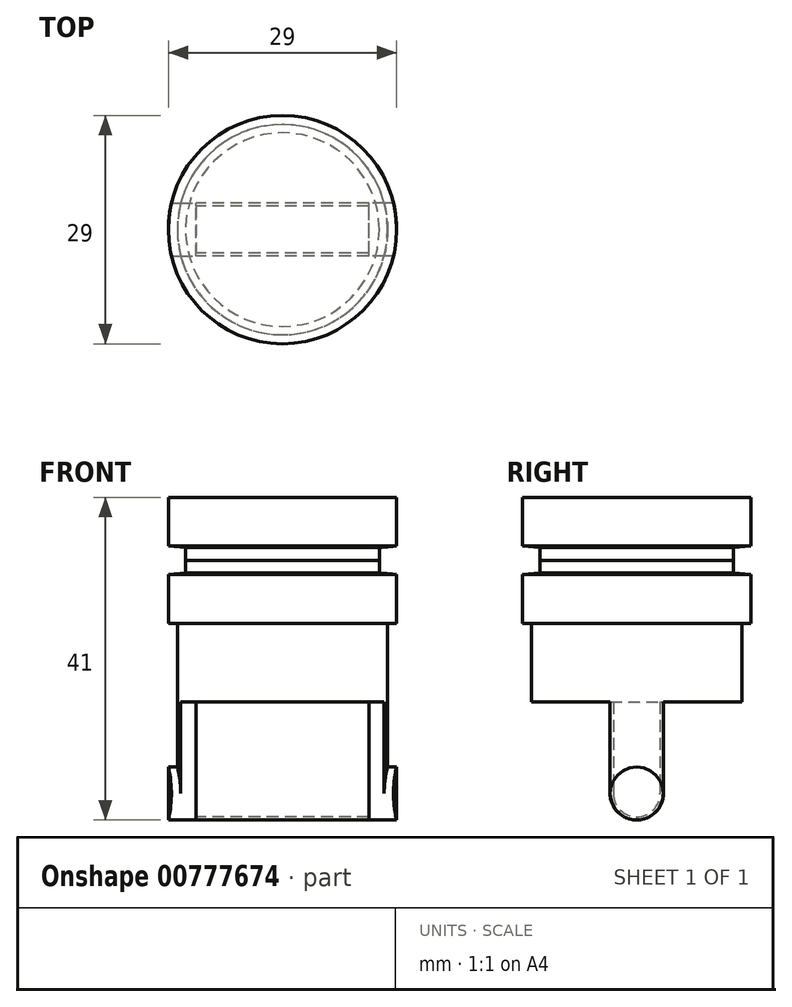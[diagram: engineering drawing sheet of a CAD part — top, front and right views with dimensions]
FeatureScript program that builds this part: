
annotation { "Feature Type Name" : "Feature", "Feature Type Description" : "" }
export const myFeature = defineFeature(function(context is Context, id is Id, definition is map)
    precondition{}
    {
        {
            var Q0;
            Q0=qCreatedBy(makeId("Top.planeOp"),FACE);
            var sketch = newSketch(context, id + "F0", { "sketchPlane" : qUnion([Q0])});
            skCircle(sketch, "E0", {"center": v(0, 0) * mm, "radius": 13.35 * mm});
            skCircle(sketch, "E1", {"center": v(0, 0) * mm, "radius": 14.5 * mm});
            skSolve(sketch);
        }
        {
            var Q0;
            Q0=makeQuery(id+"F0.imprint","IMPRINT",FACE,{"disambiguationData":[TD([[makeQuery(id+"F0.imprint","IMPRINT",EDGE,{"derivedFrom":sQuery(id+"F0.wireOp",EDGE,"E0")}),1.0]])]});
            extrude(context, id + "F1", {"entities" : qUnion([Q0]), "oppositeDirection" : true, "depth" : 10 * mm, "offsetDistance" : 25 * mm});
        }
        {
            var Q0;
            Q0=makeQuery(id+"F0.imprint","IMPRINT",FACE,{"disambiguationData":[TD([[makeQuery(id+"F0.imprint","IMPRINT",EDGE,{"derivedFrom":sQuery(id+"F0.wireOp",EDGE,"E0")}),1.0]])]});
            var Q1;
            Q1=makeQuery(id+"F0.imprint","IMPRINT",FACE,{"disambiguationData":[TD([[makeQuery(id+"F0.imprint","IMPRINT",EDGE,{"derivedFrom":sQuery(id+"F0.wireOp",EDGE,"E0")}),-1.0]])]});
            extrude(context, id + "F2", {"entities" : qUnion([Q0, Q1]), "operationType" : NewBodyOperationType.ADD, "depth" : 8 * mm, "offsetDistance" : 25 * mm});
        }
        {
            var Q0;
            Q0=makeQuery(id+"F2.opExtrude","CAP_FACE",FACE,{"disambiguationData":[OSD([sQuery(id+"F0.wireOp",EDGE,"E1")])],"isStart":false});
            extrude(context, id + "F3", {"entities" : qUnion([Q0]), "depth" : 8 * mm, "offsetDistance" : 25 * mm});
        }
        {
            var Q0;
            Q0=qCreatedBy(makeId("Front.planeOp"),FACE);
            var sketch = newSketch(context, id + "F4", { "sketchPlane" : qUnion([Q0])});
            skLineSegment(sketch, "E2.0", {"start": v(-14.5, 8) * mm, "end": v(14.5, 8) * mm});
            skLineSegment(sketch, "E3.bottom", {"start": v(-14.5, 6.18) * mm, "end": v(-12.3, 6.37) * mm});
            skLineSegment(sketch, "E3.top", {"start": v(-14.5, 9.82) * mm, "end": v(-12.3, 9.63) * mm});
            skLineSegment(sketch, "E3.left", {"start": v(-14.5, 6.18) * mm, "end": v(-14.5, 9.82) * mm});
            skLineSegment(sketch, "E3.right", {"start": v(-12.3, 6.37) * mm, "end": v(-12.3, 9.63) * mm});
            skSolve(sketch);
        }
        {
            var Q0;
            {var subQ5=sQuery(id+"F4.wireOp",EDGE,"E3.top");Q0=makeQuery(id+"F4.imprint","IMPRINT",FACE,{"disambiguationData":[TD([[makeQuery(id+"F4.imprint","IMPRINT",EDGE,{"derivedFrom":subQ5}),-1.0]])]});}
            var Q1;
            {var subQ5=sQuery(id+"F4.wireOp",EDGE,"E3.bottom");Q1=makeQuery(id+"F4.imprint","IMPRINT",FACE,{"disambiguationData":[TD([[makeQuery(id+"F4.imprint","IMPRINT",EDGE,{"derivedFrom":subQ5}),1.0]])]});}
            var Q2;
            Q2=makeQuery(id+"F2.opExtrude","CAP_EDGE",EDGE,{"disambiguationData":[OSD([sQuery(id+"F0.wireOp",EDGE,"E1")])],"isStart":false});
            revolve(context, id + "F5", {"operationType" : NewBodyOperationType.REMOVE, "surfaceOperationType" : NewSurfaceOperationType.NEW, "entities" : qUnion([Q0, Q1]), "axis" : qUnion([Q2]), "revolveType" : RevolveType.FULL, "oppositeDirection" : true});
        }
        {
            var Q0;
            Q0=qCreatedBy(makeId("Right.planeOp"),FACE);
            cPlane(context, id + "F6", {"entities" : qUnion([Q0]), "cplaneType" : CPlaneType.OFFSET, "offset" : 11 * mm, "width" : 150 * mm, "height" : 150 * mm});
        }
        {
            var Q0;
            Q0=qCreatedBy(id+"F6.planeOp",FACE);
            var sketch = newSketch(context, id + "F7", { "sketchPlane" : qUnion([Q0])});
            skLineSegment(sketch, "E4.0", {"start": v(-13.35, -10) * mm, "end": v(13.35, -10) * mm});
            skLineSegment(sketch, "E5.bottom", {"start": v(-3.38, -10) * mm, "end": v(3.38, -10) * mm});
            skLineSegment(sketch, "E5.top", {"start": v(-3.38, -25) * mm, "end": v(3.38, -25) * mm});
            skLineSegment(sketch, "E5.left", {"start": v(-3.37, -10) * mm, "end": v(-3.38, -25) * mm});
            skLineSegment(sketch, "E5.right", {"start": v(3.38, -10) * mm, "end": v(3.37, -25) * mm});
            skPoint(sketch, "E6", {"position": v(0, -25) * mm});
            skPoint(sketch, "E6.positionSnap0", {"position": v(0, -10) * mm});
            skCircle(sketch, "E7", {"center": v(0, -21.63) * mm, "radius": 3.37 * mm});
            skSolve(sketch);
        }
        {
            var Q0;
            {var subQ0=sQuery(id+"F7.wireOp",EDGE,"E5.right");var subQ1=sQuery(id+"F7.wireOp",EDGE,"E4.0");var subQ2=makeQuery(id+"F7.imprint","INTERSECT",VERTEX,{"derivedFrom":[subQ1,subQ0]});Q0=makeQuery(id+"F7.imprint","IMPRINT",FACE,{"disambiguationData":[TD([[makeQuery(id+"F7.imprint","IMPRINT",EDGE,{"disambiguationData":[TD([[subQ2,1.0]])],"derivedFrom":subQ1}),-1.0]])]});}
            var Q1;
            Q1=makeQuery(id+"F1.opExtrude","SWEPT_FACE",FACE,{"disambiguationData":[OSD([sQuery(id+"F0.wireOp",EDGE,"E0")])]});
            extrude(context, id + "F8", {"entities" : qUnion([Q0]), "endBound" : BoundingType.UP_TO_SURFACE, "depth" : 25 * mm, "endBoundEntityFace" : qUnion([Q1]), "offsetDistance" : 25 * mm});
        }
        {
            var Q0;
            {var subQ0=sQuery(id+"F7.wireOp",EDGE,"E7");var subQ1=makeQuery(id+"F7.imprint","INTERSECT",VERTEX,{"derivedFrom":[sQuery(id+"F7.wireOp",EDGE,"E5.top"),subQ0]});Q0=makeQuery(id+"F7.imprint","IMPRINT",FACE,{"disambiguationData":[TD([[makeQuery(id+"F7.imprint","IMPRINT",EDGE,{"disambiguationData":[TD([[subQ1,-1.0]])],"derivedFrom":subQ0}),1.0]])]});}
            var Q1;
            Q1=makeQuery(id+"F2.opExtrude","SWEPT_FACE",FACE,{"disambiguationData":[OSD([sQuery(id+"F0.wireOp",EDGE,"E1")])]});
            extrude(context, id + "F9", {"entities" : qUnion([Q0]), "operationType" : NewBodyOperationType.ADD, "endBound" : BoundingType.UP_TO_SURFACE, "depth" : 25 * mm, "endBoundEntityFace" : qUnion([Q1]), "offsetDistance" : 25 * mm});
        }
        {
            var Q0;
            Q0=makeQuery(id+"F8.opExtrude","SWEPT_BODY",BODY,{"disambiguationData":[OSD([sQuery(id+"F7.wireOp",EDGE,"E4.0"),sQuery(id+"F7.wireOp",EDGE,"E5.left"),sQuery(id+"F7.wireOp",EDGE,"E5.right"),sQuery(id+"F7.wireOp",EDGE,"E7")])]});
            var Q1;
            Q1=qCreatedBy(makeId("Right.planeOp"),FACE);
            mirror(context, id + "F10", {"operationType" : NewBodyOperationType.ADD, "entities" : qUnion([Q0]), "mirrorPlane" : qUnion([Q1])});
        }
        {
            var Q0;
            {var subQ0=sQuery(id+"F7.wireOp",EDGE,"E7");Q0=makeQuery(id+"F10.opPattern","COPY",FACE,{"derivedFrom":makeQuery(id+"F9.boolean.opBoolean","MERGE",FACE,{"derivedFrom":[makeQuery(id+"F8.opExtrude","CAP_FACE",FACE,{"disambiguationData":[OSD([sQuery(id+"F7.wireOp",EDGE,"E4.0"),sQuery(id+"F7.wireOp",EDGE,"E5.left"),sQuery(id+"F7.wireOp",EDGE,"E5.right"),subQ0])],"isStart":true}),makeQuery(id+"F9.opExtrude","CAP_FACE",FACE,{"disambiguationData":[OSD([subQ0])],"isStart":true})]}),"instanceName":"1"});}
            var Q1;
            {var subQ0=sQuery(id+"F7.wireOp",EDGE,"E7");Q1=makeQuery(id+"F9.boolean.opBoolean","MERGE",FACE,{"derivedFrom":[makeQuery(id+"F8.opExtrude","CAP_FACE",FACE,{"disambiguationData":[OSD([sQuery(id+"F7.wireOp",EDGE,"E4.0"),sQuery(id+"F7.wireOp",EDGE,"E5.left"),sQuery(id+"F7.wireOp",EDGE,"E5.right"),subQ0])],"isStart":true}),makeQuery(id+"F9.opExtrude","CAP_FACE",FACE,{"disambiguationData":[OSD([subQ0])],"isStart":true})]});}
            extrude(context, id + "F11", {"entities" : qUnion([Q0]), "endBound" : BoundingType.UP_TO_SURFACE, "depth" : 25 * mm, "endBoundEntityFace" : qUnion([Q1]), "offsetDistance" : 25 * mm});
        }
        {
            var Q0;
            Q0=makeQuery(id+"F11.opExtrude","SWEPT_FACE",FACE,{"disambiguationData":[OSD([sQuery(id+"F7.wireOp",EDGE,"E4.0")])]});
            var Q1;
            Q1=makeQuery(id+"F11.opExtrude","CAP_FACE",FACE,{"disambiguationData":[OSD([sQuery(id+"F7.wireOp",EDGE,"E4.0"),sQuery(id+"F7.wireOp",EDGE,"E5.left"),sQuery(id+"F7.wireOp",EDGE,"E5.right"),sQuery(id+"F7.wireOp",EDGE,"E7")])],"isStart":true});
            var Q2;
            Q2=makeQuery(id+"F11.opExtrude","CAP_FACE",FACE,{"disambiguationData":[OSD([sQuery(id+"F7.wireOp",EDGE,"E4.0"),sQuery(id+"F7.wireOp",EDGE,"E5.left"),sQuery(id+"F7.wireOp",EDGE,"E5.right"),sQuery(id+"F7.wireOp",EDGE,"E7")])],"isStart":false});
            shell(context, id + "F12", {"entities" : qUnion([Q0, Q1, Q2]), "thickness" : 0.4 * mm});
        }
    });
